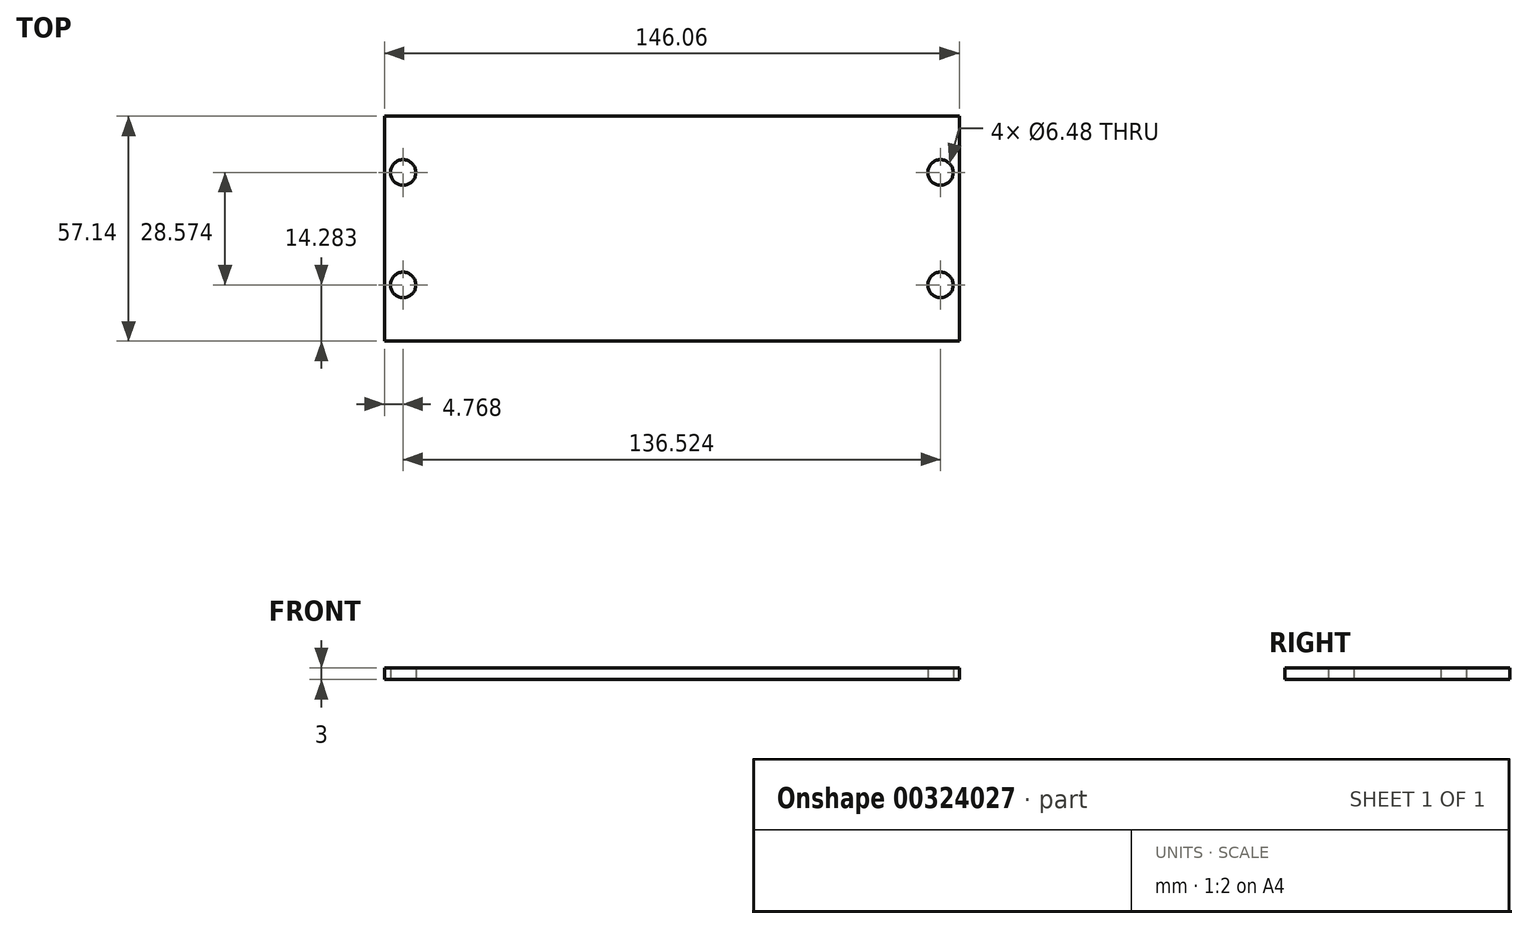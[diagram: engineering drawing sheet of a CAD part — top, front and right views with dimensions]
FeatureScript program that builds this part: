
annotation { "Feature Type Name" : "Feature", "Feature Type Description" : "" }
export const myFeature = defineFeature(function(context is Context, id is Id, definition is map)
    precondition{}
    {
        {
            var Q0;
            Q0=qCreatedBy(makeId("Top.planeOp"),FACE);
            var sketch = newSketch(context, id + "F0", { "sketchPlane" : qUnion([Q0])});
            skLineSegment(sketch, "E0", {"start": v(-68.26, 20.64) * mm, "end": v(-72.23, 20.64) * mm});
            skLineSegment(sketch, "E1", {"start": v(-72.23, 20.64) * mm, "end": v(-72.23, 27.78) * mm});
            skArc(sketch, "E2", {"start": v(-68.26, 7.94) * mm, "mid": v(-61.91, 14.29) * mm, "end": v(-68.26, 20.64) * mm});
            skLineSegment(sketch, "E3", {"start": v(-68.26, 7.94) * mm, "end": v(-72.23, 7.94) * mm});
            skLineSegment(sketch, "E4", {"start": v(-72.23, -7.94) * mm, "end": v(-72.23, 7.94) * mm});
            skLineSegment(sketch, "E5", {"start": v(72.22, 20.64) * mm, "end": v(72.22, 27.78) * mm});
            skLineSegment(sketch, "E6", {"start": v(69.24, 20.64) * mm, "end": v(72.22, 20.64) * mm});
            skArc(sketch, "E7", {"start": v(69.24, 20.64) * mm, "mid": v(62.91, 14.26) * mm, "end": v(69.29, 7.94) * mm});
            skLineSegment(sketch, "E8", {"start": v(72.22, 27.78) * mm, "end": v(-72.23, 27.78) * mm});
            skLineSegment(sketch, "E9", {"start": v(72.22, -7.94) * mm, "end": v(72.22, 7.94) * mm});
            skLineSegment(sketch, "E10", {"start": v(69.29, 7.94) * mm, "end": v(72.22, 7.94) * mm});
            skArc(sketch, "E11", {"start": v(68.18, -7.94) * mm, "mid": v(61.91, -14.37) * mm, "end": v(68.35, -20.64) * mm});
            skLineSegment(sketch, "E12", {"start": v(68.18, -7.94) * mm, "end": v(72.22, -7.94) * mm});
            skLineSegment(sketch, "E13", {"start": v(-69.22, -20.64) * mm, "end": v(-72.23, -20.64) * mm});
            skLineSegment(sketch, "E14", {"start": v(72.22, -27.77) * mm, "end": v(72.22, -20.64) * mm});
            skLineSegment(sketch, "E15", {"start": v(68.35, -20.64) * mm, "end": v(72.22, -20.64) * mm});
            skLineSegment(sketch, "E16", {"start": v(-72.23, -27.77) * mm, "end": v(-72.23, -20.64) * mm});
            skArc(sketch, "E17", {"start": v(-69.22, -20.64) * mm, "mid": v(-62.91, -14.25) * mm, "end": v(-69.3, -7.94) * mm});
            skLineSegment(sketch, "E18", {"start": v(-69.3, -7.94) * mm, "end": v(-72.23, -7.94) * mm});
            skLineSegment(sketch, "E19", {"start": v(-72.23, -27.77) * mm, "end": v(72.23, -27.77) * mm});
            skCircle(sketch, "E20", {"center": v(68.26, -14.29) * mm, "radius": 3.24 * mm});
            skCircle(sketch, "E21", {"center": v(-68.26, 14.29) * mm, "radius": 3.24 * mm});
            skLineSegment(sketch, "E22", {"start": v(-73.03, 28.57) * mm, "end": v(73.03, 28.57) * mm});
            skLineSegment(sketch, "E23", {"start": v(-73.03, -28.57) * mm, "end": v(-73.03, 28.57) * mm});
            skLineSegment(sketch, "E24", {"start": v(73.03, -28.57) * mm, "end": v(-73.03, -28.57) * mm});
            skLineSegment(sketch, "E25", {"start": v(73.03, 28.57) * mm, "end": v(73.03, -28.57) * mm});
            skCircle(sketch, "E26", {"center": v(-68.26, -14.29) * mm, "radius": 3.24 * mm});
            skCircle(sketch, "E27", {"center": v(68.26, 14.29) * mm, "radius": 3.24 * mm});
            skSolve(sketch);
        }
        {
            var Q0;
            Q0 = qSketchRegion(id + "F0", true);
            var Q1;
            Q1=makeQuery(id+"F0.imprint","IMPRINT",FACE,{"disambiguationData":[TD([[makeQuery(id+"F0.imprint","IMPRINT",EDGE,{"derivedFrom":sQuery(id+"F0.wireOp",EDGE,"E2")}),-1.0]])]});
            extrude(context, id + "F1", {"entities" : qUnion([Q0, Q1]), "depth" : 3 * mm});
        }
    });
